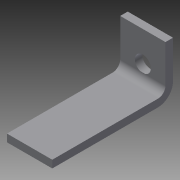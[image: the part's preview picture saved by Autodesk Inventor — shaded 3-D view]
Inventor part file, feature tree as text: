
AUTODESK INVENTOR PART (.ipt)
format: ipt  version: 2013 (Build 170138000, 138)  size: 114,688 bytes
history: native  units: in
note: dims shown in document units (in); Inventor stores cm internally (conversion verified against a paired STEP export)
features: sheet_metal_op x4, sketch x4, other x4, reference x3
ambient origin geometry x8: Origin, YZ Plane, XZ Plane, XY Plane, X Axis, Y Axis, Z Axis, Center Point
bodies: Solid1 (feature_tree)
feature tree (15):
  sheet_metal_op  "Face1"
  sheet_metal_op  "Flange1"
  sketch  "Sketch1"  dims[d0=0.875in]
  other  "Plate1"
  sketch  "Sketch2"  dims[d1=0.75in]
  other  "Plate2"
  sheet_metal_op  "Bend1"
  sheet_metal_op  "Corner1"
  sketch  "Sketch3"  dims[d2=0.125in]
  reference  "Reference1"
  reference  "Reference2"
  reference  "Reference3"
  sketch  "Sketch4"  dims[d3=0.125in d4=0.0625in d5=0.25in d6=0.125in d7=3.0in d8=90.0deg d9=0.05in d10=0.5in d11=0.125in d12=0.125in d13=0.125in d14=0.0in d15=0.5in d16=0.266in d17=0.5in d18=0.266in d19=0.125in d20=0.0in]
  other  "Cut1"
  other  "Cut2"
